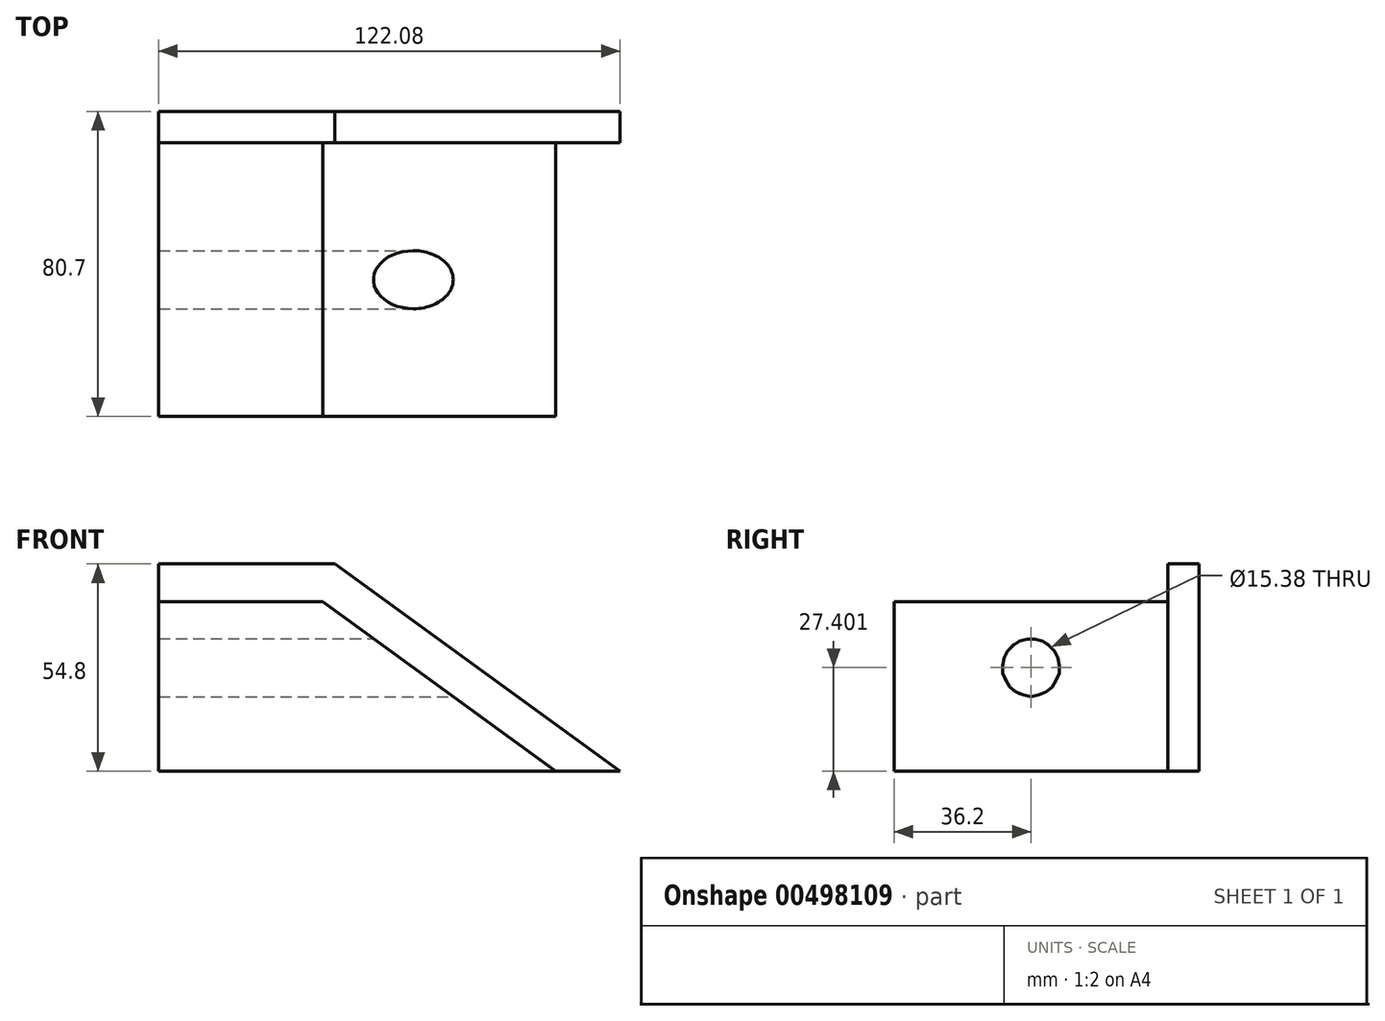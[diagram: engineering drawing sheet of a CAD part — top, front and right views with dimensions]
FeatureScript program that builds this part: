
annotation { "Feature Type Name" : "Feature", "Feature Type Description" : "" }
export const myFeature = defineFeature(function(context is Context, id is Id, definition is map)
    precondition{}
    {
        {
            var Q0;
            Q0=qCreatedBy(makeId("Front.planeOp"),FACE);
            var sketch = newSketch(context, id + "F0", { "sketchPlane" : qUnion([Q0])});
            skLineSegment(sketch, "E0", {"start": v(0, 0) * mm, "end": v(-105.07, 0) * mm});
            skLineSegment(sketch, "E1", {"start": v(-105.07, 0) * mm, "end": v(-105.07, 44.8) * mm});
            skLineSegment(sketch, "E2", {"start": v(-105.07, 44.8) * mm, "end": v(-61.65, 44.8) * mm});
            skLineSegment(sketch, "E3", {"start": v(-61.65, 44.8) * mm, "end": v(0, 0) * mm});
            skLineSegment(sketch, "E4.0", {"start": v(-58.4, 54.8) * mm, "end": v(17.01, 0) * mm});
            skLineSegment(sketch, "E4.1", {"start": v(-105.07, 54.8) * mm, "end": v(-58.4, 54.8) * mm});
            skLineSegment(sketch, "E5", {"start": v(0, 0) * mm, "end": v(17.01, 0) * mm});
            skLineSegment(sketch, "E6", {"start": v(-105.07, 54.8) * mm, "end": v(-105.07, 44.8) * mm});
            skSolve(sketch);
        }
        {
            var Q0;
            Q0=makeQuery(id+"F0.imprint","IMPRINT",FACE,{"disambiguationData":[TD([[makeQuery(id+"F0.imprint","IMPRINT",EDGE,{"derivedFrom":sQuery(id+"F0.wireOp",EDGE,"E0")}),-1.0]])]});
            extrude(context, id + "F1", {"entities" : qUnion([Q0]), "depth" : 80.7 * mm});
        }
        {
            var Q0;
            Q0=makeQuery(id+"F0.imprint","IMPRINT",FACE,{"disambiguationData":[TD([[makeQuery(id+"F0.imprint","IMPRINT",EDGE,{"derivedFrom":sQuery(id+"F0.wireOp",EDGE,"E2")}),1.0]])]});
            extrude(context, id + "F2", {"entities" : qUnion([Q0]), "operationType" : NewBodyOperationType.ADD, "depth" : 8.3 * mm});
        }
        {
            var Q0;
            Q0=qCreatedBy(makeId("Right.planeOp"),FACE);
            var sketch = newSketch(context, id + "F3", { "sketchPlane" : qUnion([Q0])});
            skPoint(sketch, "E7.0", {"position": v(-44.5, 44.8) * mm});
            skPoint(sketch, "E8.0", {"position": v(-8.3, 27.4) * mm});
            skCircle(sketch, "E9", {"center": v(-44.5, 27.4) * mm, "radius": 7.69 * mm});
            skSolve(sketch);
        }
        {
            var Q0;
            Q0 = qSketchRegion(id + "F3", true);
            extrude(context, id + "F4", {"entities" : qUnion([Q0]), "operationType" : NewBodyOperationType.REMOVE, "endBound" : BoundingType.THROUGH_ALL, "oppositeDirection" : true, "depth" : 25 * mm});
        }
    });
